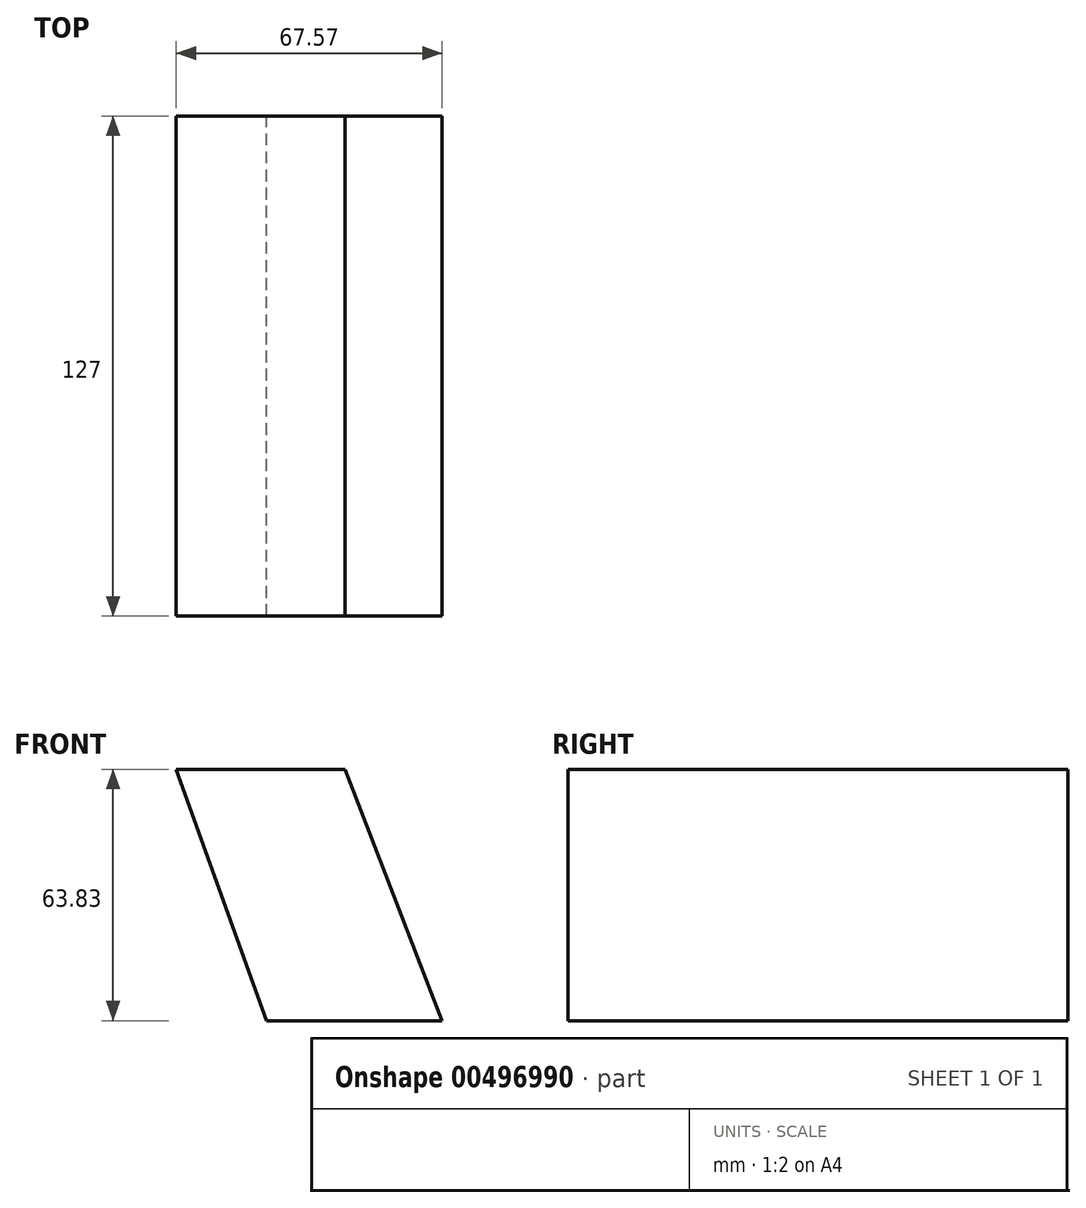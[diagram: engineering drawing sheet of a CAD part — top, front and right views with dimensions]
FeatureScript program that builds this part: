
annotation { "Feature Type Name" : "Feature", "Feature Type Description" : "" }
export const myFeature = defineFeature(function(context is Context, id is Id, definition is map)
    precondition{}
    {
        {
            var Q0;
            Q0=qCreatedBy(makeId("Front.planeOp"),FACE);
            var sketch = newSketch(context, id + "F0", { "sketchPlane" : qUnion([Q0])});
            skLineSegment(sketch, "E0", {"start": v(-47.53, 39.14) * mm, "end": v(-4.66, 39.14) * mm});
            skLineSegment(sketch, "E1", {"start": v(-47.53, 39.14) * mm, "end": v(-24.53, -24.7) * mm});
            skLineSegment(sketch, "E2", {"start": v(-24.53, -24.7) * mm, "end": v(20.04, -24.7) * mm});
            skLineSegment(sketch, "E3", {"start": v(-4.66, 39.14) * mm, "end": v(20.04, -24.7) * mm});
            skSolve(sketch);
        }
        {
            var Q0;
            Q0=makeQuery(id+"F0.imprint","IMPRINT",FACE,{"disambiguationData":[TD([[makeQuery(id+"F0.imprint","IMPRINT",EDGE,{"derivedFrom":sQuery(id+"F0.wireOp",EDGE,"E0")}),-1.0]])]});
            extrude(context, id + "F1", {"entities" : qUnion([Q0]), "endBound" : BoundingType.SYMMETRIC, "depth" : 127 * mm});
        }
    });
